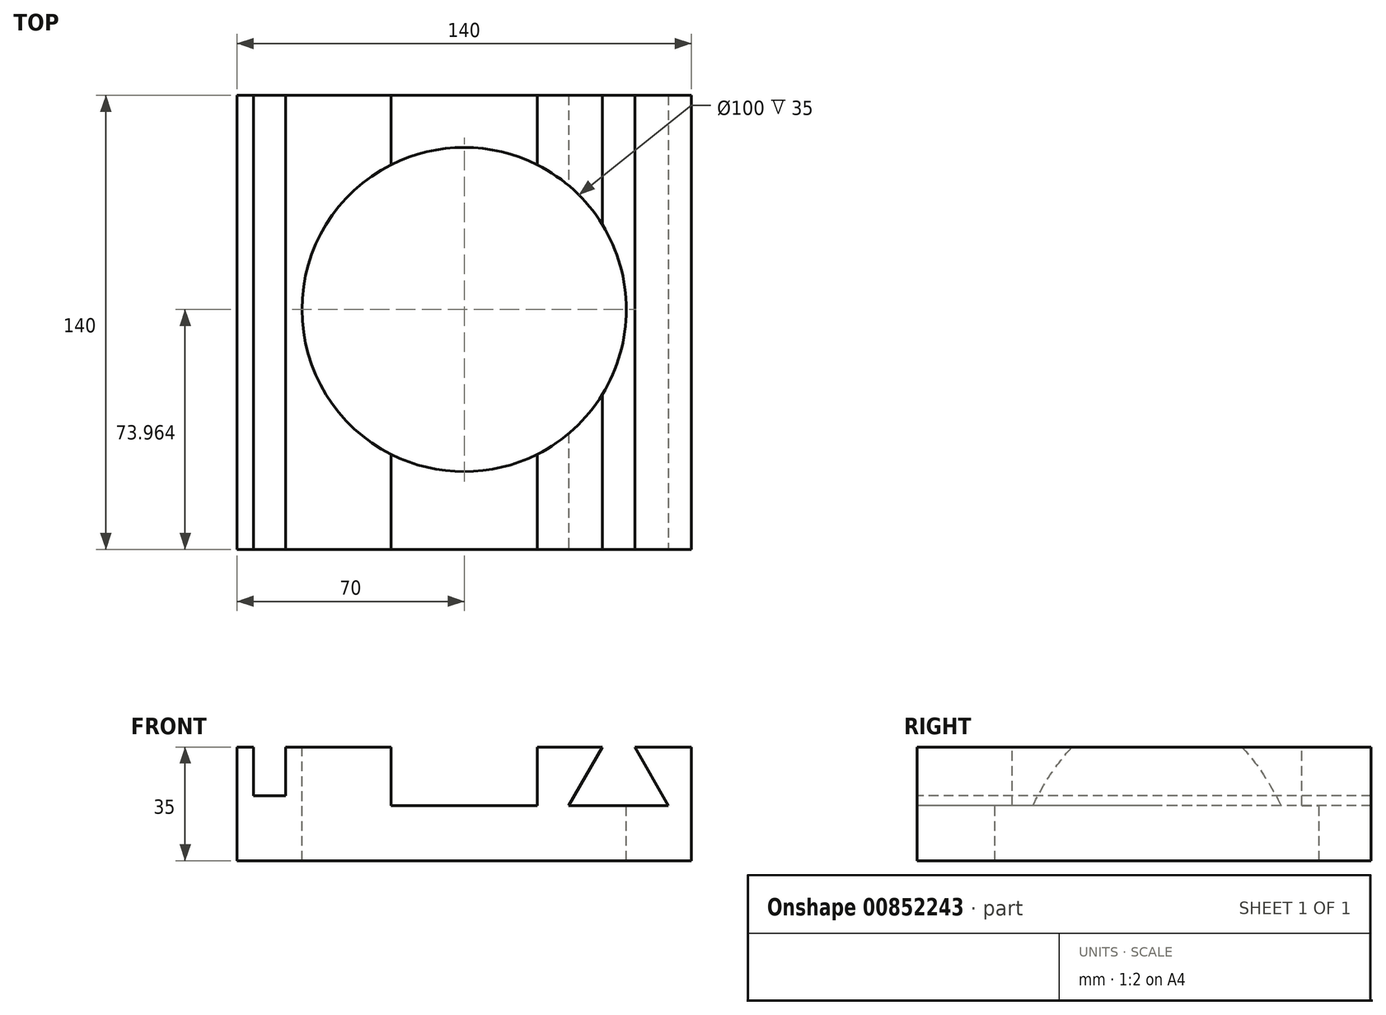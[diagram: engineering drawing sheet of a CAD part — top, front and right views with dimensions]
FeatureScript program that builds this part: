
annotation { "Feature Type Name" : "Feature", "Feature Type Description" : "" }
export const myFeature = defineFeature(function(context is Context, id is Id, definition is map)
    precondition{}
    {
        {
            var Q0;
            Q0=qCreatedBy(makeId("Top.planeOp"),FACE);
            var sketch = newSketch(context, id + "F0", { "sketchPlane" : qUnion([Q0])});
            skLineSegment(sketch, "E0.bottom", {"start": v(70, -70) * mm, "end": v(-70, -70) * mm});
            skLineSegment(sketch, "E0.top", {"start": v(70, 70) * mm, "end": v(-70, 70) * mm});
            skLineSegment(sketch, "E0.left", {"start": v(70, -70) * mm, "end": v(70, 70) * mm});
            skLineSegment(sketch, "E0.right", {"start": v(-70, -70) * mm, "end": v(-70, 70) * mm});
            skPoint(sketch, "E0.middle", {"position": v(0, 0) * mm});
            skCircle(sketch, "E1", {"center": v(0, 3.96) * mm, "radius": 50 * mm});
            skSolve(sketch);
        }
        {
            var Q0;
            Q0=makeQuery(id+"F0.imprint","IMPRINT",FACE,{"disambiguationData":[TD([[makeQuery(id+"F0.imprint","IMPRINT",EDGE,{"derivedFrom":sQuery(id+"F0.wireOp",EDGE,"E0.bottom")}),-1.0]])]});
            extrude(context, id + "F1", {"entities" : qUnion([Q0]), "endBound" : BoundingType.SYMMETRIC, "oppositeDirection" : true, "depth" : 35 * mm, "offsetDistance" : 25 * mm});
        }
        {
            var Q0;
            Q0=makeQuery(id+"F1.opExtrude","CAP_FACE",FACE,{"disambiguationData":[OSD([sQuery(id+"F0.wireOp",EDGE,"E0.bottom"),sQuery(id+"F0.wireOp",EDGE,"E0.top"),sQuery(id+"F0.wireOp",EDGE,"E0.left"),sQuery(id+"F0.wireOp",EDGE,"E0.right"),sQuery(id+"F0.wireOp",EDGE,"E1")])],"isStart":true});
            var sketch = newSketch(context, id + "F2", { "sketchPlane" : qUnion([Q0])});
            skLineSegment(sketch, "E2", {"start": v(-65, 70) * mm, "end": v(-65, -70) * mm});
            skLineSegment(sketch, "E3", {"start": v(-65, -70) * mm, "end": v(-55, -70) * mm});
            skLineSegment(sketch, "E4", {"start": v(-55, -70) * mm, "end": v(-55, 70) * mm});
            skLineSegment(sketch, "E5", {"start": v(-55, 70) * mm, "end": v(-65, 70) * mm});
            skSolve(sketch);
        }
        {
            var Q0;
            Q0=makeQuery(id+"F2.imprint","IMPRINT",FACE,{"disambiguationData":[TD([[makeQuery(id+"F2.imprint","IMPRINT",EDGE,{"derivedFrom":sQuery(id+"F2.wireOp",EDGE,"E2")}),1.0]])]});
            extrude(context, id + "F3", {"entities" : qUnion([Q0]), "operationType" : NewBodyOperationType.REMOVE, "oppositeDirection" : true, "depth" : 15 * mm, "offsetDistance" : 25 * mm});
        }
        {
            var Q0;
            {var subQ0=sQuery(id+"F0.wireOp",EDGE,"E1");var subQ1=sQuery(id+"F0.wireOp",EDGE,"E0.left");var subQ2=sQuery(id+"F0.wireOp",EDGE,"E0.top");var subQ3=sQuery(id+"F0.wireOp",EDGE,"E0.bottom");Q0=makeQuery(id+"F3.boolean.opBoolean","SPLIT",FACE,{"disambiguationData":[TD([makeQuery(id+"F1.opExtrude","SWEPT_FACE",FACE,{"disambiguationData":[OSD([subQ1])]})])],"derivedFrom":makeQuery(id+"F1.opExtrude","CAP_FACE",FACE,{"disambiguationData":[OSD([subQ3,subQ2,subQ1,sQuery(id+"F0.wireOp",EDGE,"E0.right"),subQ0])],"isStart":true})});}
            var sketch = newSketch(context, id + "F4", { "sketchPlane" : qUnion([Q0])});
            skLineSegment(sketch, "E6", {"start": v(22.5, 70) * mm, "end": v(22.5, -70) * mm});
            skLineSegment(sketch, "E7", {"start": v(22.5, -70) * mm, "end": v(-22.5, -70) * mm});
            skLineSegment(sketch, "E8", {"start": v(-22.5, -70) * mm, "end": v(-22.5, 70) * mm});
            skLineSegment(sketch, "E9", {"start": v(-22.5, 70) * mm, "end": v(22.5, 70) * mm});
            skLineSegment(sketch, "E10", {"start": v(0, 70) * mm, "end": v(0, -70) * mm, "construction": true});
            skPoint(sketch, "E11", {"position": v(0, 0) * mm});
            skSolve(sketch);
        }
        {
            var Q0;
            {var subQ0=sQuery(id+"F4.wireOp",EDGE,"E7");Q0=makeQuery(id+"F4.imprint","IMPRINT",FACE,{"disambiguationData":[TD([[makeQuery(id+"F4.imprint","IMPRINT",EDGE,{"derivedFrom":subQ0}),-1.0]])]});}
            var Q1;
            {var subQ0=sQuery(id+"F4.wireOp",EDGE,"E9");Q1=makeQuery(id+"F4.imprint","IMPRINT",FACE,{"disambiguationData":[TD([[makeQuery(id+"F4.imprint","IMPRINT",EDGE,{"derivedFrom":subQ0}),1.0]])]});}
            extrude(context, id + "F5", {"entities" : qUnion([Q0, Q1]), "operationType" : NewBodyOperationType.REMOVE, "oppositeDirection" : true, "depth" : 18 * mm, "offsetDistance" : 25 * mm});
        }
        {
            var Q0;
            Q0=makeQuery(id+"F1.opExtrude","SWEPT_FACE",FACE,{"disambiguationData":[OSD([sQuery(id+"F0.wireOp",EDGE,"E0.bottom")])]});
            var sketch = newSketch(context, id + "F6", { "sketchPlane" : qUnion([Q0])});
            skLineSegment(sketch, "E12", {"start": v(42.6, 17.5) * mm, "end": v(32.2, -0.5) * mm});
            skLineSegment(sketch, "E13", {"start": v(32.2, -0.5) * mm, "end": v(62.99, -0.5) * mm});
            skLineSegment(sketch, "E14", {"start": v(62.99, -0.5) * mm, "end": v(52.6, 17.5) * mm});
            skLineSegment(sketch, "E15", {"start": v(52.6, 17.5) * mm, "end": v(42.6, 17.5) * mm});
            skLineSegment(sketch, "E16", {"start": v(0, -0.5) * mm, "end": v(0, 35.08) * mm, "construction": true});
            skLineSegment(sketch, "E17", {"start": v(47.6, -0.5) * mm, "end": v(47.6, 30.64) * mm, "construction": true});
            skSolve(sketch);
        }
        {
            var Q0;
            Q0=makeQuery(id+"F6.imprint","IMPRINT",FACE,{"disambiguationData":[TD([[makeQuery(id+"F6.imprint","IMPRINT",EDGE,{"derivedFrom":sQuery(id+"F6.wireOp",EDGE,"E12")}),1.0]])]});
            extrude(context, id + "F7", {"entities" : qUnion([Q0]), "operationType" : NewBodyOperationType.REMOVE, "oppositeDirection" : true, "depth" : 172.6 * mm, "offsetDistance" : 25 * mm});
        }
    });
